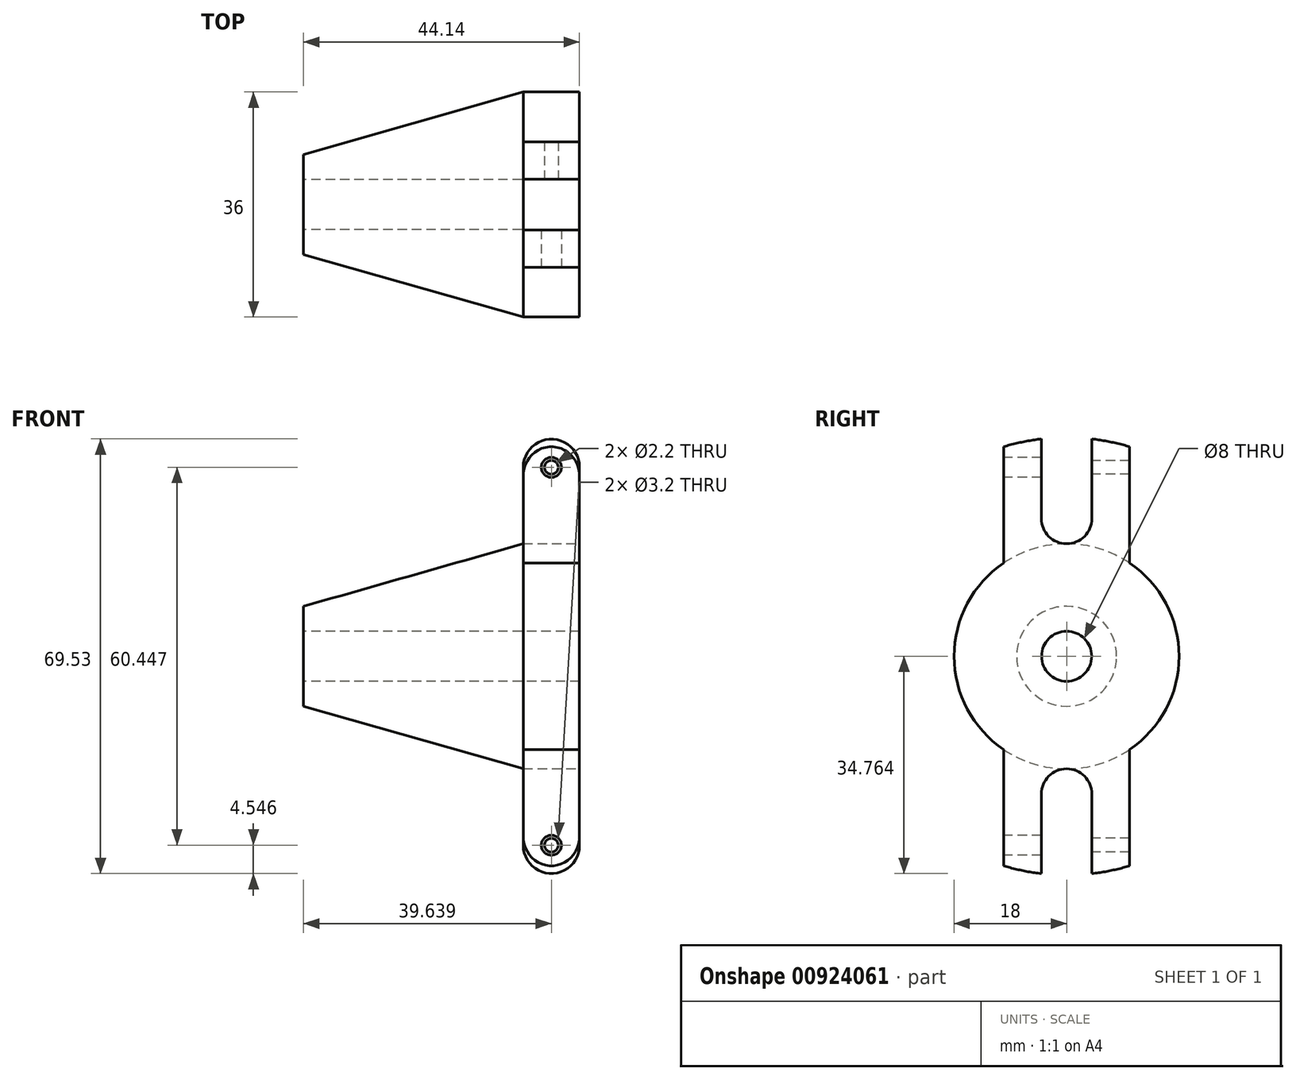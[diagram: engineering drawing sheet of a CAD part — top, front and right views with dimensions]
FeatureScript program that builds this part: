
annotation { "Feature Type Name" : "Feature", "Feature Type Description" : "" }
export const myFeature = defineFeature(function(context is Context, id is Id, definition is map)
    precondition{}
    {
        {
            var Q0;
            Q0=qCreatedBy(makeId("Front.planeOp"),FACE);
            var sketch = newSketch(context, id + "F0", { "sketchPlane" : qUnion([Q0])});
            skLineSegment(sketch, "E0", {"start": v(-22.43, 4) * mm, "end": v(21.7, 4) * mm});
            skLineSegment(sketch, "E1", {"start": v(21.7, 4) * mm, "end": v(21.7, 35) * mm});
            skLineSegment(sketch, "E2", {"start": v(21.7, 35) * mm, "end": v(12.7, 35) * mm});
            skLineSegment(sketch, "E3", {"start": v(-22.43, 8) * mm, "end": v(-22.43, 4) * mm});
            skLineSegment(sketch, "E4", {"start": v(12.7, 35) * mm, "end": v(12.7, 18) * mm});
            skLineSegment(sketch, "E5", {"start": v(12.7, 18) * mm, "end": v(-22.43, 8) * mm});
            skLineSegment(sketch, "E6", {"start": v(-71.73, 0) * mm, "end": v(96.24, 0) * mm, "construction": true});
            skSolve(sketch);
        }
        {
            var Q0;
            Q0 = qSketchRegion(id + "F0", true);
            var Q1;
            Q1=sQuery(id+"F0.wireOp",EDGE,"E6");
            revolve(context, id + "F1", {"surfaceOperationType" : NewSurfaceOperationType.NEW, "entities" : qUnion([Q0]), "axis" : qUnion([Q1]), "revolveType" : RevolveType.FULL});
        }
        {
            var Q0;
            Q0=makeQuery(id+"F1.opRevolve","SWEPT_EDGE",EDGE,{"disambiguationData":[OSD([sQuery(id+"F0.wireOp",EDGE,"E1"),sQuery(id+"F0.wireOp",EDGE,"E2")])]});
            var Q1;
            Q1=makeQuery(id+"F1.opRevolve","SWEPT_EDGE",EDGE,{"disambiguationData":[OSD([sQuery(id+"F0.wireOp",EDGE,"E2"),sQuery(id+"F0.wireOp",EDGE,"E4")])]});
            fillet(context, id + "F2", {"entities" : qUnion([Q0, Q1]), "radius" : 4.5 * mm, "tangentPropagation" : true, "allowEdgeOverflow" : false});
        }
        {
            var Q0;
            Q0=makeQuery(id+"F1.opRevolve","SWEPT_FACE",FACE,{"disambiguationData":[OSD([sQuery(id+"F0.wireOp",EDGE,"E1")])]});
            var sketch = newSketch(context, id + "F3", { "sketchPlane" : qUnion([Q0])});
            skLineSegment(sketch, "E7.bottom", {"start": v(-4.05, 39.3) * mm, "end": v(4.05, 39.3) * mm});
            skLineSegment(sketch, "E7.left", {"start": v(-4.05, 39.3) * mm, "end": v(-4.05, 22.04) * mm});
            skLineSegment(sketch, "E7.right", {"start": v(4.05, 39.3) * mm, "end": v(4.05, 22.04) * mm});
            skArc(sketch, "E8", {"start": v(-4.05, 22.04) * mm, "mid": v(0, 18) * mm, "end": v(4.05, 22.04) * mm});
            skLineSegment(sketch, "E9", {"start": v(0, 0) * mm, "end": v(57.65, 0) * mm, "construction": true});
            skLineSegment(sketch, "E10.MirrorCS", {"start": v(4.05, -39.32) * mm, "end": v(4.05, -22.06) * mm});
            skLineSegment(sketch, "E11.MirrorCS", {"start": v(-4.05, -39.32) * mm, "end": v(4.05, -39.32) * mm});
            skArc(sketch, "E12.MirrorCS", {"start": v(-4.05, -22.06) * mm, "mid": v(0, -18) * mm, "end": v(4.05, -22.06) * mm});
            skLineSegment(sketch, "E13.MirrorCS", {"start": v(-4.05, -39.32) * mm, "end": v(-4.05, -22.06) * mm});
            skArc(sketch, "E14.0", {"start": v(-10.05, -14.94) * mm, "mid": v(-18, 0) * mm, "end": v(-10.05, 14.93) * mm});
            skLineSegment(sketch, "E15", {"start": v(-10.05, 35.24) * mm, "end": v(-10.05, 14.93) * mm});
            skArc(sketch, "E16", {"start": v(-10.05, 35.24) * mm, "mid": v(-36.65, 0) * mm, "end": v(-10.05, -35.25) * mm});
            skLineSegment(sketch, "E17.trimOffspring", {"start": v(-10.05, -14.94) * mm, "end": v(-10.05, -35.25) * mm});
            skLineSegment(sketch, "E18", {"start": v(0, 27.62) * mm, "end": v(0, -17.09) * mm, "construction": true});
            skLineSegment(sketch, "E19.MirrorCS", {"start": v(10.05, -14.94) * mm, "end": v(10.05, -35.25) * mm});
            skLineSegment(sketch, "E20.MirrorCS", {"start": v(10.05, 35.24) * mm, "end": v(10.05, 14.93) * mm});
            skArc(sketch, "E21.MirrorCS", {"start": v(10.05, -14.94) * mm, "mid": v(18, 0) * mm, "end": v(10.05, 14.93) * mm});
            skArc(sketch, "E22.MirrorCS", {"start": v(10.05, 35.24) * mm, "mid": v(36.65, 0) * mm, "end": v(10.05, -35.25) * mm});
            skArc(sketch, "E23", {"start": v(10.05, 14.93) * mm, "mid": v(-14.93, 10.04) * mm, "end": v(-10.05, -14.94) * mm, "construction": true});
            skSolve(sketch);
        }
        {
            var Q0;
            Q0 = qSketchRegion(id + "F3", true);
            extrude(context, id + "F4", {"entities" : qUnion([Q0]), "operationType" : NewBodyOperationType.REMOVE, "oppositeDirection" : true, "depth" : 25 * mm, "offsetDistance" : 25 * mm});
        }
        {
            var Q0;
            Q0=makeQuery(id+"F4.boolean.opBoolean","COPY",FACE,{"derivedFrom":makeQuery(id+"F4.opExtrude","SWEPT_FACE",FACE,{"disambiguationData":[OSD([sQuery(id+"F3.wireOp",EDGE,"E15")])]})});
            var sketch = newSketch(context, id + "F5", { "sketchPlane" : qUnion([Q0])});
            skLineSegment(sketch, "E24.0", {"start": v(12.7, 30.22) * mm, "end": v(12.7, 22.04) * mm, "construction": true});
            skFitSpline(sketch, "E25.0", {"points": [v(12.7, 30.22) * mm, v(12.7, 30.52) * mm, v(12.77, 31.12) * mm, v(12.98, 31.82) * mm, v(13.23, 32.36) * mm, v(13.46, 32.74) * mm, v(13.72, 33.1) * mm, v(14.01, 33.43) * mm, v(14.34, 33.73) * mm, v(14.7, 34) * mm, v(15.08, 34.23) * mm, v(15.62, 34.48) * mm, v(16.32, 34.7) * mm, v(17.06, 34.77) * mm, v(17.65, 34.74) * mm, v(18.09, 34.68) * mm, v(18.52, 34.57) * mm, v(18.94, 34.42) * mm, v(19.34, 34.23) * mm, v(19.72, 34) * mm, v(20.08, 33.73) * mm, v(20.4, 33.43) * mm, v(20.7, 33.1) * mm, v(21.05, 32.62) * mm, v(21.32, 32.1) * mm, v(21.52, 31.54) * mm, v(21.67, 30.96) * mm, v(21.7, 30.52) * mm, v(21.7, 30.22) * mm], "construction": true});
            skLineSegment(sketch, "E26.0", {"start": v(21.7, 30.22) * mm, "end": v(21.7, 22.04) * mm, "construction": true});
            skLineSegment(sketch, "E27", {"start": v(12.7, 30.22) * mm, "end": v(21.7, 30.22) * mm, "construction": true});
            skPoint(sketch, "E28", {"position": v(17.2, 30.22) * mm});
            skLineSegment(sketch, "E29.MirrorCS", {"start": v(12.7, -30.22) * mm, "end": v(12.7, -22.04) * mm, "construction": true});
            skFitSpline(sketch, "E30.MirrorCS", {"points": [v(12.7, -30.22) * mm, v(12.7, -30.52) * mm, v(12.77, -31.12) * mm, v(12.98, -31.82) * mm, v(13.23, -32.36) * mm, v(13.46, -32.74) * mm, v(13.72, -33.1) * mm, v(14.01, -33.43) * mm, v(14.34, -33.73) * mm, v(14.7, -34) * mm, v(15.08, -34.23) * mm, v(15.62, -34.48) * mm, v(16.32, -34.7) * mm, v(17.06, -34.77) * mm, v(17.65, -34.74) * mm, v(18.09, -34.68) * mm, v(18.52, -34.57) * mm, v(18.94, -34.42) * mm, v(19.34, -34.23) * mm, v(19.72, -34) * mm, v(20.08, -33.73) * mm, v(20.4, -33.43) * mm, v(20.7, -33.1) * mm, v(21.05, -32.62) * mm, v(21.32, -32.1) * mm, v(21.52, -31.54) * mm, v(21.67, -30.96) * mm, v(21.7, -30.52) * mm, v(21.7, -30.22) * mm], "construction": true});
            skLineSegment(sketch, "E31.MirrorCS", {"start": v(12.7, -30.22) * mm, "end": v(21.7, -30.22) * mm, "construction": true});
            skLineSegment(sketch, "E32.MirrorCS", {"start": v(21.7, -30.22) * mm, "end": v(21.7, -22.04) * mm, "construction": true});
            skPoint(sketch, "E33.MirrorP", {"position": v(17.2, -30.22) * mm});
            skSolve(sketch);
        }
        {
            var Q0;
            Q0=sQuery(id+"F5.wireOp",VERTEX,"E28");
            var Q1;
            Q1=sQuery(id+"F5.wireOp",VERTEX,"E33.MirrorP");
            var Q2;
            Q2=makeQuery(id+"F1.opRevolve","SWEPT_BODY",BODY,{"disambiguationData":[OSD([sQuery(id+"F0.wireOp",EDGE,"E0"),sQuery(id+"F0.wireOp",EDGE,"E1"),sQuery(id+"F0.wireOp",EDGE,"E2"),sQuery(id+"F0.wireOp",EDGE,"E3"),sQuery(id+"F0.wireOp",EDGE,"E4"),sQuery(id+"F0.wireOp",EDGE,"E5")])]});
            hole(context, id + "F6", {"style" : HoleStyle.C_BORE, "endStyle" : HoleEndStyle.THROUGH, "holeDiameter" : 2.2 * mm, "cBoreDiameter" : 3.2 * mm, "cBoreDepth" : 6 * mm, "majorDiameter" : 5 * mm, "isTappedThrough" : true, "tappedDepth" : 20.5 * mm, "tapClearance" : 3, "locations" : qUnion([Q0, Q1]), "scope" : qUnion([Q2])});
        }
    });
